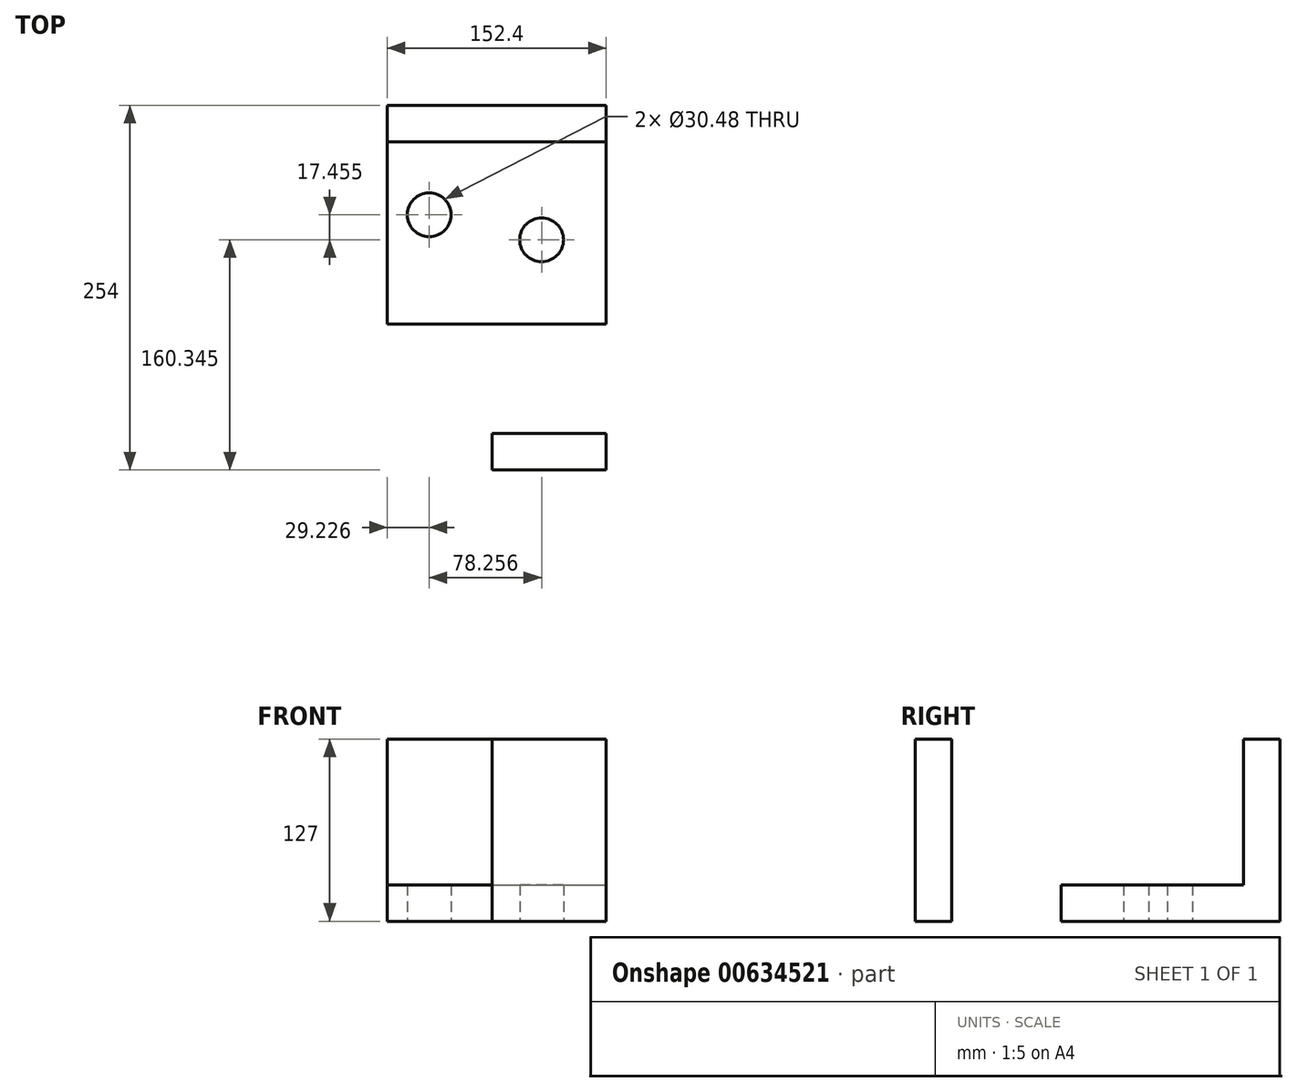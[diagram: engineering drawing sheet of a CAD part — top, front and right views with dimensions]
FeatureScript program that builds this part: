
annotation { "Feature Type Name" : "Feature", "Feature Type Description" : "" }
export const myFeature = defineFeature(function(context is Context, id is Id, definition is map)
    precondition{}
    {
        {
            var Q0;
            Q0=qCreatedBy(makeId("Top.planeOp"),FACE);
            var sketch = newSketch(context, id + "F0", { "sketchPlane" : qUnion([Q0])});
            skLineSegment(sketch, "E0.bottom", {"start": v(-72.88, 76.2) * mm, "end": v(79.52, 76.2) * mm});
            skLineSegment(sketch, "E0.top", {"start": v(-72.88, -76.2) * mm, "end": v(79.52, -76.2) * mm});
            skLineSegment(sketch, "E0.left", {"start": v(-72.88, 76.2) * mm, "end": v(-72.88, -76.2) * mm});
            skLineSegment(sketch, "E0.right", {"start": v(79.52, 76.2) * mm, "end": v(79.52, -76.2) * mm});
            skLineSegment(sketch, "E1.bottom", {"start": v(0, -76.2) * mm, "end": v(79.52, -76.2) * mm});
            skLineSegment(sketch, "E1.top", {"start": v(0, -177.8) * mm, "end": v(79.52, -177.8) * mm});
            skLineSegment(sketch, "E1.left", {"start": v(0, -76.2) * mm, "end": v(0, -177.8) * mm});
            skLineSegment(sketch, "E1.right", {"start": v(79.52, -76.2) * mm, "end": v(79.52, -177.8) * mm});
            skLineSegment(sketch, "E2", {"start": v(-72.88, 50.8) * mm, "end": v(79.52, 50.8) * mm});
            skLineSegment(sketch, "E3", {"start": v(0, -152.4) * mm, "end": v(79.52, -152.4) * mm});
            skCircle(sketch, "E4", {"center": v(-43.65, 0) * mm, "radius": 15.24 * mm});
            skCircle(sketch, "E5", {"center": v(34.6, -17.46) * mm, "radius": 15.24 * mm});
            skSolve(sketch);
        }
        {
            var Q0;
            {var subQ0=sQuery(id+"F0.wireOp",EDGE,"E0.bottom");Q0=makeQuery(id+"F0.imprint","IMPRINT",FACE,{"disambiguationData":[TD([[makeQuery(id+"F0.imprint","IMPRINT",EDGE,{"derivedFrom":subQ0}),-1.0]])]});}
            extrude(context, id + "F1", {"entities" : qUnion([Q0]), "depth" : 127 * mm, "offsetDistance" : 25.4 * mm});
        }
        {
            var Q0;
            {var subQ4=sQuery(id+"F0.wireOp",EDGE,"E0.top");Q0=makeQuery(id+"F0.imprint","IMPRINT",FACE,{"disambiguationData":[TD([[makeQuery(id+"F0.imprint","IMPRINT",EDGE,{"derivedFrom":subQ4}),1.0]])]});}
            var Q1;
            {var subQ0=sQuery(id+"F0.wireOp",EDGE,"E1.bottom");Q1=makeQuery(id+"F0.imprint","IMPRINT",FACE,{"disambiguationData":[TD([[makeQuery(id+"F0.imprint","IMPRINT",EDGE,{"derivedFrom":subQ0}),-1.0]])]});}
            extrude(context, id + "F2", {"entities" : qUnion([Q0, Q1]), "operationType" : NewBodyOperationType.ADD, "depth" : 25.4 * mm, "offsetDistance" : 25.4 * mm});
        }
        {
            var Q0;
            {var subQ0=sQuery(id+"F0.wireOp",EDGE,"E1.top");Q0=makeQuery(id+"F0.imprint","IMPRINT",FACE,{"disambiguationData":[TD([[makeQuery(id+"F0.imprint","IMPRINT",EDGE,{"derivedFrom":subQ0}),1.0]])]});}
            extrude(context, id + "F3", {"entities" : qUnion([Q0]), "operationType" : NewBodyOperationType.ADD, "depth" : 127 * mm, "offsetDistance" : 25.4 * mm});
        }
    });
